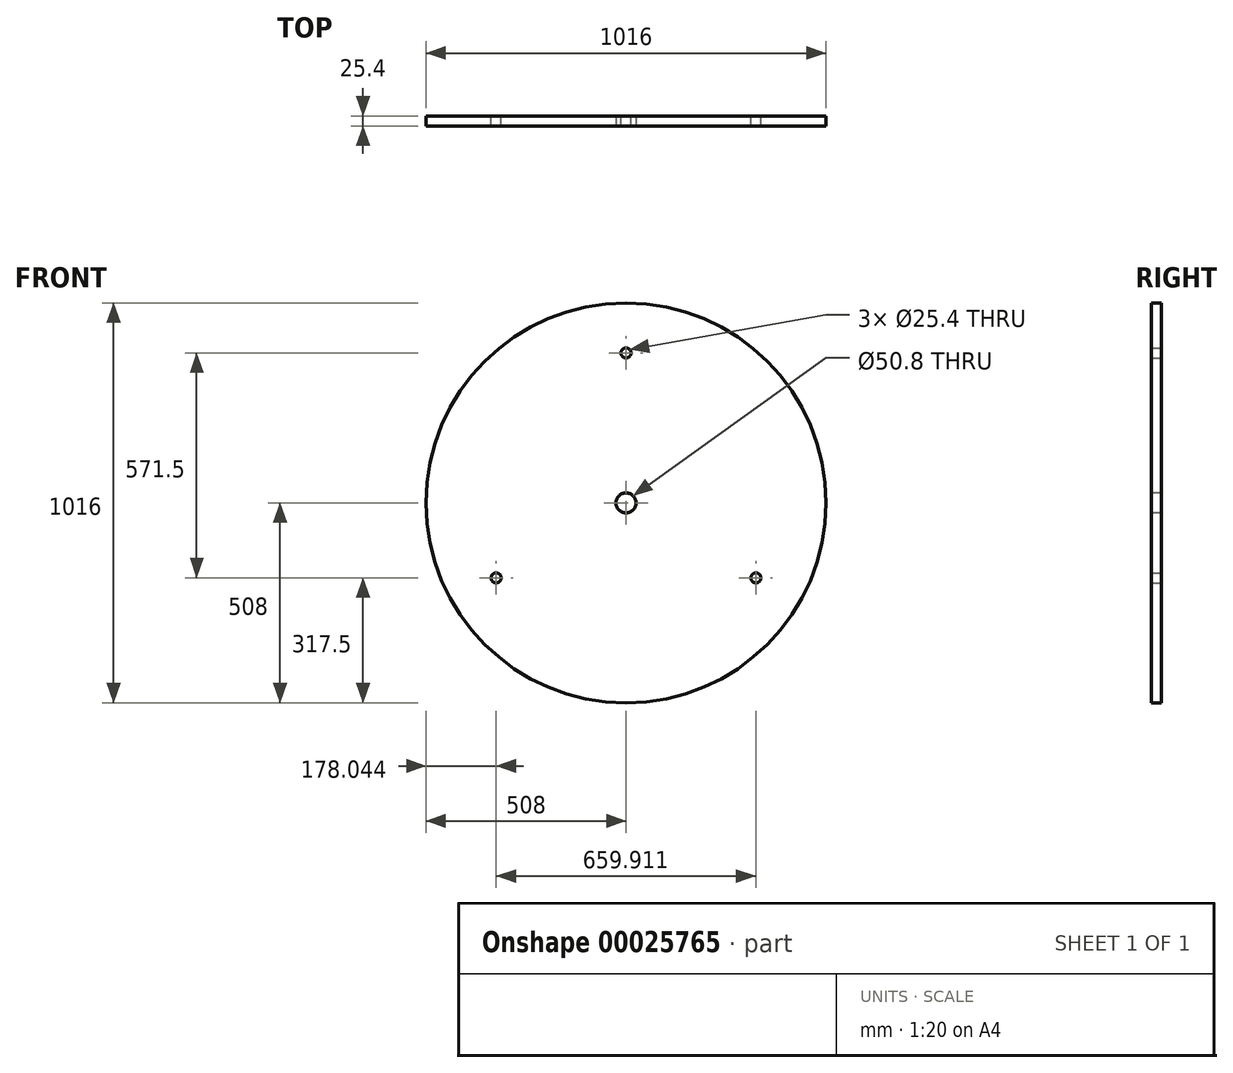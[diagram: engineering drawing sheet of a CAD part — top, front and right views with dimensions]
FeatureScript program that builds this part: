
annotation { "Feature Type Name" : "Feature", "Feature Type Description" : "" }
export const myFeature = defineFeature(function(context is Context, id is Id, definition is map)
    precondition{}
    {
        {
            var Q0;
            Q0=qCreatedBy(makeId("Front.planeOp"),FACE);
            var sketch = newSketch(context, id + "F0", { "sketchPlane" : qUnion([Q0])});
            skCircle(sketch, "E0", {"center": v(0, 0) * mm, "radius": 508 * mm});
            skCircle(sketch, "E1", {"center": v(0, 0) * mm, "radius": 381 * mm, "construction": true});
            skCircle(sketch, "E2", {"center": v(0, 381) * mm, "radius": 12.7 * mm});
            skCircle(sketch, "E3.1.0", {"center": v(-329.96, -190.5) * mm, "radius": 12.7 * mm});
            skCircle(sketch, "E3.2.0", {"center": v(329.96, -190.5) * mm, "radius": 12.7 * mm});
            skSolve(sketch);
        }
        {
            var Q0;
            Q0 = qSketchRegion(id + "F0", true);
            extrude(context, id + "F1", {"entities" : qUnion([Q0]), "depth" : 25.4 * mm});
        }
        {
            var Q0;
            Q0=makeQuery(id+"F1.opExtrude","CAP_FACE",FACE,{"disambiguationData":[OSD([sQuery(id+"F0.wireOp",EDGE,"E0"),sQuery(id+"F0.wireOp",EDGE,"E2"),sQuery(id+"F0.wireOp",EDGE,"E3.1.0"),sQuery(id+"F0.wireOp",EDGE,"E3.2.0")])],"isStart":false});
            var sketch = newSketch(context, id + "F2", { "sketchPlane" : qUnion([Q0])});
            skCircle(sketch, "E4", {"center": v(0, 0) * mm, "radius": 25.4 * mm});
            skSolve(sketch);
        }
        {
            var Q0;
            Q0=sQuery(id+"F2.wireOp",VERTEX,"E4.center");
            var Q1;
            Q1=makeQuery(id+"F1.opExtrude","SWEPT_BODY",BODY,{"disambiguationData":[OSD([sQuery(id+"F0.wireOp",EDGE,"E0"),sQuery(id+"F0.wireOp",EDGE,"E2"),sQuery(id+"F0.wireOp",EDGE,"E3.1.0"),sQuery(id+"F0.wireOp",EDGE,"E3.2.0")])]});
            hole(context, id + "F3", {"style" : HoleStyle.SIMPLE, "holeDiameter" : 50.8 * mm, "endStyle" : HoleEndStyle.THROUGH, "locations" : qUnion([Q0]), "scope" : qUnion([Q1])});
        }
    });
